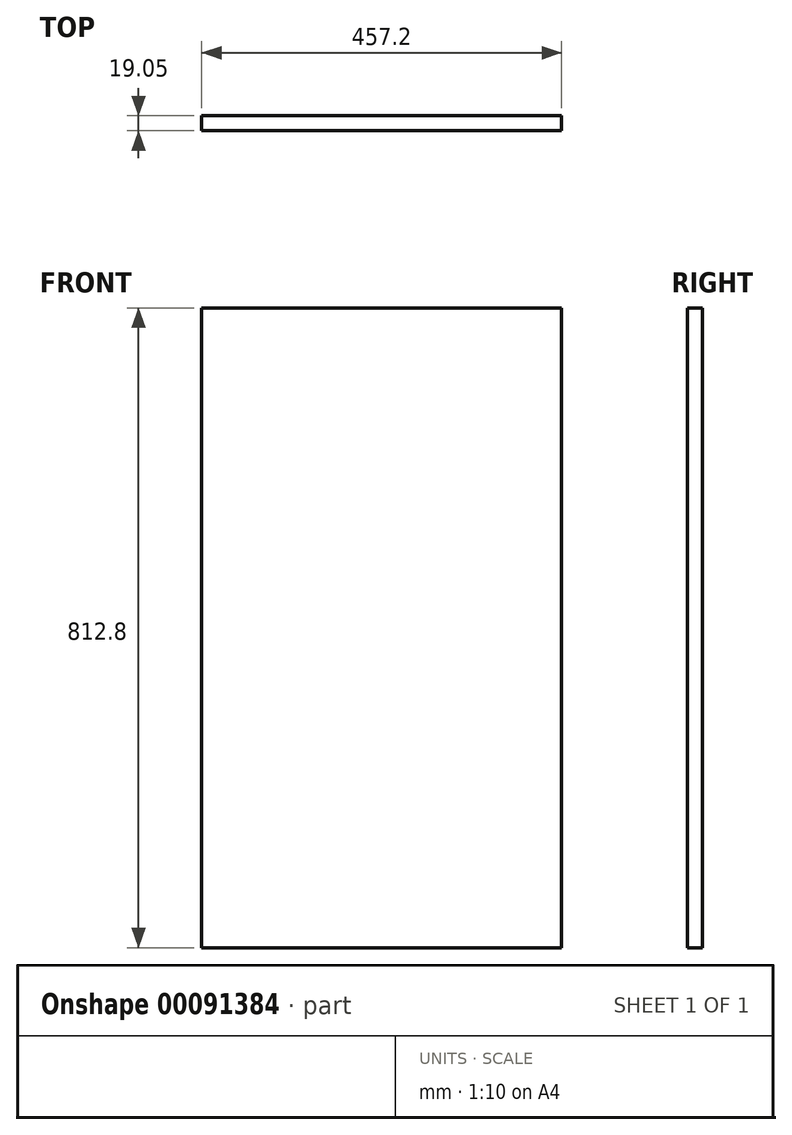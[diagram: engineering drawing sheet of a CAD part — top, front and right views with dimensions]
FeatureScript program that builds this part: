
annotation { "Feature Type Name" : "Feature", "Feature Type Description" : "" }
export const myFeature = defineFeature(function(context is Context, id is Id, definition is map)
    precondition{}
    {
        {
            var Q0;
            Q0=qCreatedBy(makeId("Front.planeOp"),FACE);
            var sketch = newSketch(context, id + "F0", { "sketchPlane" : qUnion([Q0])});
            skLineSegment(sketch, "E0.bottom", {"start": v(-228.6, 406.4) * mm, "end": v(228.6, 406.4) * mm});
            skLineSegment(sketch, "E0.top", {"start": v(-228.6, -406.4) * mm, "end": v(228.6, -406.4) * mm});
            skLineSegment(sketch, "E0.left", {"start": v(-228.6, 406.4) * mm, "end": v(-228.6, -406.4) * mm});
            skLineSegment(sketch, "E0.right", {"start": v(228.6, 406.4) * mm, "end": v(228.6, -406.4) * mm});
            skPoint(sketch, "E0.middle", {"position": v(0, 0) * mm});
            skSolve(sketch);
        }
        {
            var Q0;
            Q0=makeQuery(id+"F0.imprint","IMPRINT",FACE,{"disambiguationData":[TD([[makeQuery(id+"F0.imprint","IMPRINT",EDGE,{"derivedFrom":sQuery(id+"F0.wireOp",EDGE,"E0.bottom")}),-1.0]])]});
            extrude(context, id + "F1", {"entities" : qUnion([Q0]), "oppositeDirection" : true, "depth" : 19.05 * mm});
        }
    });
